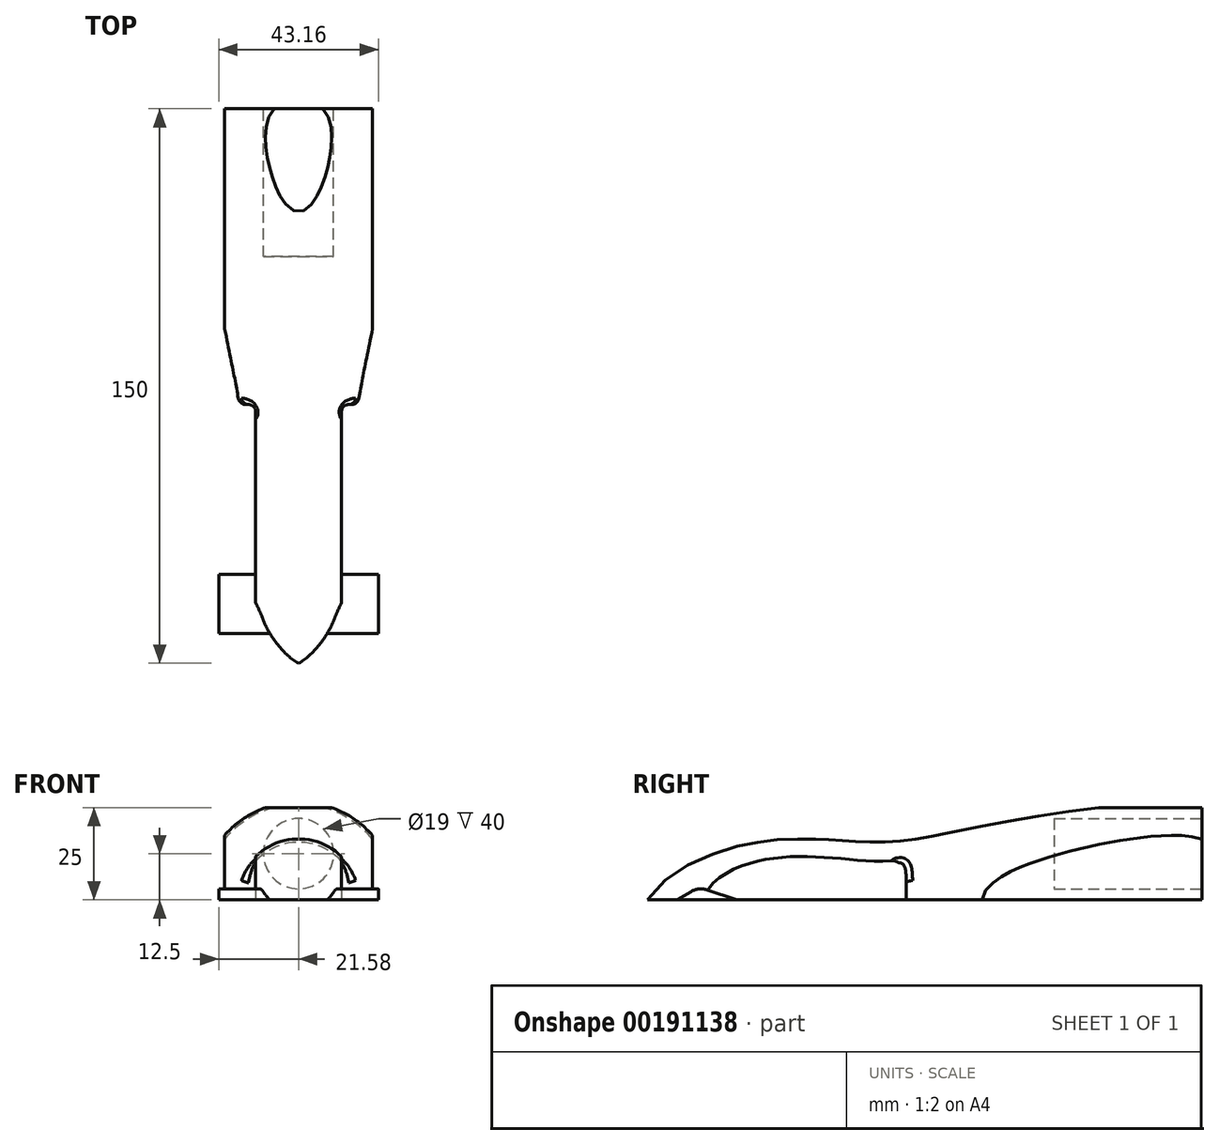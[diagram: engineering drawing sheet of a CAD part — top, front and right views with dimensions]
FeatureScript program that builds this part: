
annotation { "Feature Type Name" : "Feature", "Feature Type Description" : "" }
export const myFeature = defineFeature(function(context is Context, id is Id, definition is map)
    precondition{}
    {
        {
            var Q0;
            Q0=qCreatedBy(makeId("Right.planeOp"),FACE);
            var sketch = newSketch(context, id + "F0", { "sketchPlane" : qUnion([Q0])});
            skLineSegment(sketch, "E0", {"start": v(0, 0) * mm, "end": v(150, 0) * mm});
            skFitSpline(sketch, "E1", {"points": [v(0, 0) * mm, v(23.8, 14.36) * mm, v(48.96, 16.28) * mm, v(66.47, 15.73) * mm, v(90.54, 20) * mm, v(150, 25.85) * mm], "startDerivative": vector(55.26, 100.69) * mm, "endDerivative": vector(97.95, -26.68) * mm});
            skLineSegment(sketch, "E2", {"start": v(150, 0) * mm, "end": v(150, 25.85) * mm});
            skSolve(sketch);
        }
        {
            var Q0;
            Q0 = qSketchRegion(id + "F0", true);
            var Q1;
            Q1=sQuery(id+"F0.wireOp",EDGE,"E0");
            revolve(context, id + "F1", {"entities" : qUnion([Q0]), "axis" : qUnion([Q1]), "revolveType" : RevolveType.SYMMETRIC, "angle" : 180 * degree});
        }
        {
            var Q0;
            Q0=qCreatedBy(makeId("Front.planeOp"),FACE);
            var sketch = newSketch(context, id + "F2", { "sketchPlane" : qUnion([Q0])});
            skLineSegment(sketch, "E3.bottom", {"start": v(-20, 0) * mm, "end": v(0, 0) * mm});
            skLineSegment(sketch, "E3.top", {"start": v(-20, 25) * mm, "end": v(0, 25) * mm});
            skLineSegment(sketch, "E3.left", {"start": v(-20, 0) * mm, "end": v(-20, 25) * mm});
            skLineSegment(sketch, "E3.right", {"start": v(0, 0) * mm, "end": v(0, 25) * mm});
            skLineSegment(sketch, "E4.MirrorCS", {"start": v(20, 0) * mm, "end": v(20, 25) * mm});
            skLineSegment(sketch, "E5.MirrorCS", {"start": v(20, 25) * mm, "end": v(0, 25) * mm});
            skLineSegment(sketch, "E6.MirrorCS", {"start": v(20, 0) * mm, "end": v(0, 0) * mm});
            skLineSegment(sketch, "E7", {"start": v(-20, 0) * mm, "end": v(-36.62, 0) * mm});
            skLineSegment(sketch, "E8", {"start": v(-36.62, 0) * mm, "end": v(-36.62, 34.87) * mm});
            skLineSegment(sketch, "E9", {"start": v(-36.62, 34.87) * mm, "end": v(32.85, 34.87) * mm});
            skLineSegment(sketch, "E10", {"start": v(32.85, 34.87) * mm, "end": v(32.85, 0) * mm});
            skLineSegment(sketch, "E11", {"start": v(32.85, 0) * mm, "end": v(20, 0) * mm});
            skSolve(sketch);
        }
        {
            var Q0;
            Q0=makeQuery(id+"F2.imprint","IMPRINT",FACE,{"disambiguationData":[TD([[makeQuery(id+"F2.imprint","IMPRINT",EDGE,{"derivedFrom":sQuery(id+"F2.wireOp",EDGE,"E3.top")}),1.0]])]});
            extrude(context, id + "F3", {"entities" : qUnion([Q0]), "operationType" : NewBodyOperationType.REMOVE, "endBound" : BoundingType.THROUGH_ALL, "oppositeDirection" : true, "depth" : 134 * mm});
        }
        {
            var Q0;
            Q0=qCreatedBy(makeId("Front.planeOp"),FACE);
            var sketch = newSketch(context, id + "F4", { "sketchPlane" : qUnion([Q0])});
            skLineSegment(sketch, "E12", {"start": v(0, 0) * mm, "end": v(-11.58, 0) * mm});
            skLineSegment(sketch, "E13", {"start": v(-11.58, 0) * mm, "end": v(-11.58, 15.75) * mm});
            skLineSegment(sketch, "E14", {"start": v(-11.58, 15.75) * mm, "end": v(-22.35, 15.75) * mm});
            skLineSegment(sketch, "E15", {"start": v(-22.35, 15.75) * mm, "end": v(-22.35, 0) * mm});
            skLineSegment(sketch, "E16", {"start": v(-22.35, 0) * mm, "end": v(-11.58, 0) * mm});
            skLineSegment(sketch, "E17", {"start": v(0, 0) * mm, "end": v(0, 24.9) * mm, "construction": true});
            skLineSegment(sketch, "E18.MirrorCS", {"start": v(22.35, 0) * mm, "end": v(11.58, 0) * mm});
            skLineSegment(sketch, "E19.MirrorCS", {"start": v(11.58, 0) * mm, "end": v(11.58, 15.75) * mm});
            skLineSegment(sketch, "E20.MirrorCS", {"start": v(11.58, 15.75) * mm, "end": v(22.35, 15.75) * mm});
            skLineSegment(sketch, "E21.MirrorCS", {"start": v(22.35, 15.75) * mm, "end": v(22.35, 0) * mm});
            skSolve(sketch);
        }
        {
            var Q0;
            Q0=makeQuery(id+"F4.imprint","IMPRINT",FACE,{"disambiguationData":[TD([[makeQuery(id+"F4.imprint","IMPRINT",EDGE,{"derivedFrom":sQuery(id+"F4.wireOp",EDGE,"E13")}),1.0]])]});
            var Q1;
            Q1=makeQuery(id+"F4.imprint","IMPRINT",FACE,{"disambiguationData":[TD([[makeQuery(id+"F4.imprint","IMPRINT",EDGE,{"derivedFrom":sQuery(id+"F4.wireOp",EDGE,"E18.MirrorCS")}),-1.0]])]});
            extrude(context, id + "F5", {"entities" : qUnion([Q0, Q1]), "operationType" : NewBodyOperationType.REMOVE, "oppositeDirection" : true, "depth" : 70 * mm});
        }
        {
            var Q0;
            Q0=makeQuery(id+"F5.boolean.opBoolean","INTERSECT",EDGE,{"derivedFrom":[makeQuery(id+"F1.opRevolve","SWEPT_FACE",FACE,{"disambiguationData":[OSD([sQuery(id+"F0.wireOp",EDGE,"E1")])]}),makeQuery(id+"F5.opExtrude","CAP_FACE",FACE,{"disambiguationData":[OSD([sQuery(id+"F4.wireOp",EDGE,"E13"),sQuery(id+"F4.wireOp",EDGE,"E14"),sQuery(id+"F4.wireOp",EDGE,"E15"),sQuery(id+"F4.wireOp",EDGE,"E16")])],"isStart":false})]});
            var Q1;
            Q1=makeQuery(id+"F5.boolean.opBoolean","COPY",EDGE,{"derivedFrom":makeQuery(id+"F5.opExtrude","CAP_EDGE",EDGE,{"disambiguationData":[OSD([sQuery(id+"F4.wireOp",EDGE,"E13")])],"isStart":false})});
            var Q2;
            Q2=makeQuery(id+"F5.boolean.opBoolean","INTERSECT",EDGE,{"derivedFrom":[makeQuery(id+"F1.opRevolve","SWEPT_FACE",FACE,{"disambiguationData":[OSD([sQuery(id+"F0.wireOp",EDGE,"E1")])]}),makeQuery(id+"F5.opExtrude","CAP_FACE",FACE,{"disambiguationData":[OSD([sQuery(id+"F4.wireOp",EDGE,"E18.MirrorCS"),sQuery(id+"F4.wireOp",EDGE,"E19.MirrorCS"),sQuery(id+"F4.wireOp",EDGE,"E20.MirrorCS"),sQuery(id+"F4.wireOp",EDGE,"E21.MirrorCS")])],"isStart":false})]});
            var Q3;
            Q3=makeQuery(id+"F5.boolean.opBoolean","COPY",EDGE,{"derivedFrom":makeQuery(id+"F5.opExtrude","CAP_EDGE",EDGE,{"disambiguationData":[OSD([sQuery(id+"F4.wireOp",EDGE,"E19.MirrorCS")])],"isStart":false})});
            fillet(context, id + "F6", {"entities" : qUnion([Q0, Q1, Q2, Q3]), "radius" : 2 * mm, "tangentPropagation" : true, "allowEdgeOverflow" : false});
        }
        {
            var Q0;
            Q0=makeQuery(id+"F5.boolean.opBoolean","COPY",FACE,{"derivedFrom":makeQuery(id+"F5.opExtrude","SWEPT_FACE",FACE,{"disambiguationData":[OSD([sQuery(id+"F4.wireOp",EDGE,"E13")])]})});
            var sketch = newSketch(context, id + "F7", { "sketchPlane" : qUnion([Q0])});
            skLineSegment(sketch, "E22", {"start": v(-13.78, 3.48) * mm, "end": v(-24.12, 0) * mm});
            skLineSegment(sketch, "E23", {"start": v(-24.12, 0) * mm, "end": v(-8.07, 0) * mm});
            skLineSegment(sketch, "E24", {"start": v(-8.07, 0) * mm, "end": v(-13.78, 3.48) * mm});
            skSolve(sketch);
        }
        {
            var Q0;
            Q0 = qSketchRegion(id + "F7", true);
            extrude(context, id + "F8", {"entities" : qUnion([Q0]), "operationType" : NewBodyOperationType.ADD, "depth" : 10 * mm, "hasSecondDirection" : true, "secondDirectionOppositeDirection" : true, "secondDirectionDepth" : 8.9 * mm});
        }
        {
            var Q0;
            Q0=makeQuery(id+"F1.opRevolve","SWEPT_BODY",BODY,{"disambiguationData":[OSD([sQuery(id+"F0.wireOp",EDGE,"E0"),sQuery(id+"F0.wireOp",EDGE,"E1"),sQuery(id+"F0.wireOp",EDGE,"E2")])]});
            var Q1;
            Q1=qCreatedBy(makeId("Right.planeOp"),FACE);
            mirror(context, id + "F9", {"operationType" : NewBodyOperationType.ADD, "entities" : qUnion([Q0]), "mirrorPlane" : qUnion([Q1])});
        }
        {
            var Q0;
            Q0=makeQuery(id+"F8.opExtrude","SWEPT_EDGE",EDGE,{"disambiguationData":[OSD([sQuery(id+"F7.wireOp",EDGE,"OeARmJ3k-VEzA-hwj7-xxfW-jE6lZTBxDjzx"),sQuery(id+"F7.wireOp",EDGE,"E22")])]});
            var Q1;
            Q1=makeQuery(id+"F9.opPattern","COPY",EDGE,{"derivedFrom":makeQuery(id+"F8.opExtrude","SWEPT_EDGE",EDGE,{"disambiguationData":[OSD([sQuery(id+"F7.wireOp",EDGE,"OeARmJ3k-VEzA-hwj7-xxfW-jE6lZTBxDjzx"),sQuery(id+"F7.wireOp",EDGE,"E22")])]}),"instanceName":"1"});
            fillet(context, id + "F10", {"entities" : qUnion([Q0, Q1]), "radius" : 5 * mm, "tangentPropagation" : true, "allowEdgeOverflow" : false});
        }
        {
            var Q0;
            Q0=makeQuery(id+"F1.opRevolve","SWEPT_FACE",FACE,{"disambiguationData":[OSD([sQuery(id+"F0.wireOp",EDGE,"E2")])]});
            var sketch = newSketch(context, id + "F11", { "sketchPlane" : qUnion([Q0])});
            skLineSegment(sketch, "E25", {"start": v(0, 0) * mm, "end": v(0, 25) * mm, "construction": true});
            skCircle(sketch, "E26", {"center": v(0, 12.5) * mm, "radius": 9.5 * mm});
            skSolve(sketch);
        }
        {
            var Q0;
            Q0=makeQuery(id+"F11.imprint","IMPRINT",FACE,{"disambiguationData":[TD([[makeQuery(id+"F11.imprint","IMPRINT",EDGE,{"derivedFrom":sQuery(id+"F11.wireOp",EDGE,"E26")}),1.0]])]});
            extrude(context, id + "F12", {"entities" : qUnion([Q0]), "operationType" : NewBodyOperationType.REMOVE, "oppositeDirection" : true, "depth" : 40 * mm});
        }
    });
